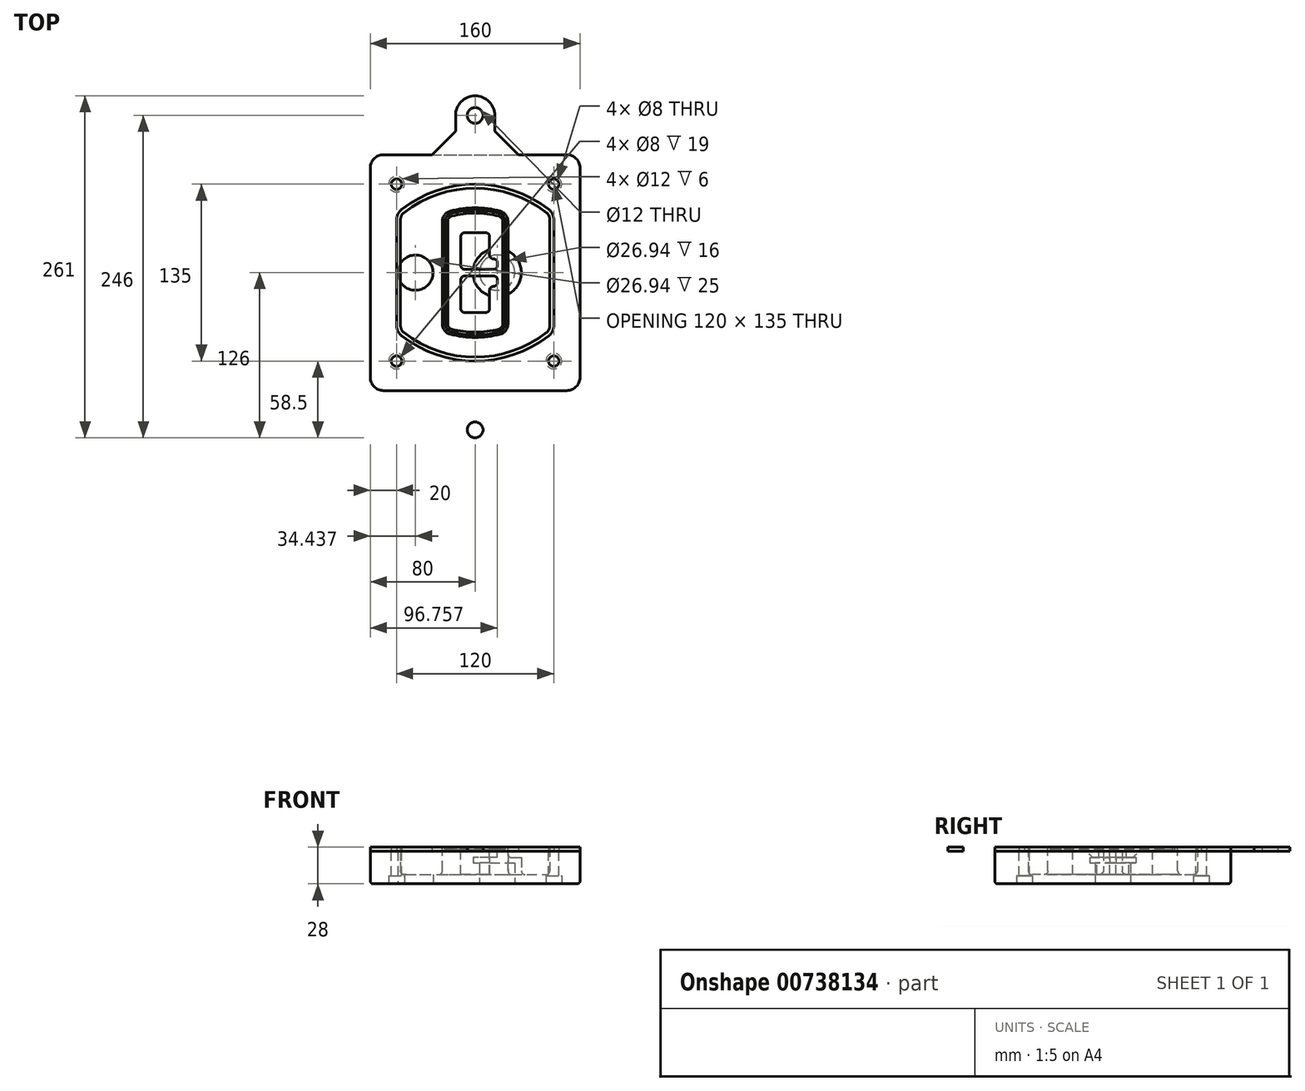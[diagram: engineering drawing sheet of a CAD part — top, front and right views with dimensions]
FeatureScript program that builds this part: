
annotation { "Feature Type Name" : "Feature", "Feature Type Description" : "" }
export const myFeature = defineFeature(function(context is Context, id is Id, definition is map)
    precondition{}
    {
        {
            var Q0;
            Q0=qCreatedBy(makeId("Top.planeOp"),FACE);
            var sketch = newSketch(context, id + "F0", { "sketchPlane" : qUnion([Q0])});
            skPoint(sketch, "E0.rect.middle", {"position": v(0, 0) * mm});
            skLineSegment(sketch, "E1.bottom", {"start": v(-70, -90) * mm, "end": v(70, -90) * mm});
            skLineSegment(sketch, "E1.top", {"start": v(-70, 90) * mm, "end": v(70, 90) * mm});
            skLineSegment(sketch, "E1.left", {"start": v(-80, -80) * mm, "end": v(-80, 80) * mm});
            skLineSegment(sketch, "E1.right", {"start": v(80, -80) * mm, "end": v(80, 80) * mm});
            skLineSegment(sketch, "E2", {"start": v(-80, 90) * mm, "end": v(80, -90) * mm, "construction": true});
            skLineSegment(sketch, "E3", {"start": v(80, 90) * mm, "end": v(-80, -90) * mm, "construction": true});
            skCircle(sketch, "E4", {"center": v(-60, 67.5) * mm, "radius": 4 * mm});
            skCircle(sketch, "E5", {"center": v(60, 67.5) * mm, "radius": 4 * mm});
            skCircle(sketch, "E6", {"center": v(60, -67.5) * mm, "radius": 4 * mm});
            skCircle(sketch, "E7", {"center": v(-60, -67.5) * mm, "radius": 4 * mm});
            skLineSegment(sketch, "E8", {"start": v(-60, 67.5) * mm, "end": v(60, 67.5) * mm, "construction": true});
            skLineSegment(sketch, "E9", {"start": v(60, 67.5) * mm, "end": v(60, -67.5) * mm, "construction": true});
            skLineSegment(sketch, "E10", {"start": v(60, -67.5) * mm, "end": v(-60, -67.5) * mm, "construction": true});
            skLineSegment(sketch, "E11", {"start": v(-60, -67.5) * mm, "end": v(-60, 67.5) * mm, "construction": true});
            skLineSegment(sketch, "E12", {"start": v(-60, 40.3) * mm, "end": v(-60, -40.3) * mm});
            skLineSegment(sketch, "E13", {"start": v(60, 40.3) * mm, "end": v(60, -40.3) * mm});
            skArc(sketch, "E14", {"start": v(56.15, 48.18) * mm, "mid": v(0, 67.5) * mm, "end": v(-56.15, 48.18) * mm});
            skArc(sketch, "E15", {"start": v(-56.15, -48.18) * mm, "mid": v(0, -67.5) * mm, "end": v(56.15, -48.18) * mm});
            skLineSegment(sketch, "E16", {"start": v(-60, 0) * mm, "end": v(60, 0) * mm, "construction": true});
            skPoint(sketch, "E17.visualSharp", {"position": v(-60, -45) * mm});
            skArc(sketch, "E17.filletArc", {"start": v(-60, -40.3) * mm, "mid": v(-58.99, -44.68) * mm, "end": v(-56.15, -48.18) * mm});
            skPoint(sketch, "E18.visualSharp", {"position": v(-60, 45) * mm});
            skArc(sketch, "E18.filletArc", {"start": v(-56.15, 48.18) * mm, "mid": v(-58.99, 44.68) * mm, "end": v(-60, 40.3) * mm});
            skPoint(sketch, "E19.visualSharp", {"position": v(60, 45) * mm});
            skArc(sketch, "E19.filletArc", {"start": v(60, 40.3) * mm, "mid": v(58.99, 44.68) * mm, "end": v(56.15, 48.18) * mm});
            skPoint(sketch, "E20.visualSharp", {"position": v(60, -45) * mm});
            skArc(sketch, "E20.filletArc", {"start": v(56.15, -48.18) * mm, "mid": v(58.99, -44.68) * mm, "end": v(60, -40.3) * mm});
            skPoint(sketch, "E21.visualSharp", {"position": v(-80, 90) * mm});
            skArc(sketch, "E21.filletArc", {"start": v(-70, 90) * mm, "mid": v(-77.07, 87.07) * mm, "end": v(-80, 80) * mm});
            skPoint(sketch, "E22.visualSharp", {"position": v(80, 90) * mm});
            skArc(sketch, "E22.filletArc", {"start": v(80, 80) * mm, "mid": v(77.07, 87.07) * mm, "end": v(70, 90) * mm});
            skPoint(sketch, "E23.visualSharp", {"position": v(80, -90) * mm});
            skArc(sketch, "E23.filletArc", {"start": v(70, -90) * mm, "mid": v(77.07, -87.07) * mm, "end": v(80, -80) * mm});
            skPoint(sketch, "E24.visualSharp", {"position": v(-80, -90) * mm});
            skArc(sketch, "E24.filletArc", {"start": v(-80, -80) * mm, "mid": v(-77.07, -87.07) * mm, "end": v(-70, -90) * mm});
            skArc(sketch, "E25.0", {"start": v(57, 40.3) * mm, "mid": v(56.3, 43.36) * mm, "end": v(54.3, 45.81) * mm});
            skLineSegment(sketch, "E25.1", {"start": v(57, 40.3) * mm, "end": v(57, -40.3) * mm});
            skArc(sketch, "E25.2", {"start": v(54.3, -45.81) * mm, "mid": v(56.3, -43.36) * mm, "end": v(57, -40.3) * mm});
            skArc(sketch, "E25.3", {"start": v(-54.3, -45.81) * mm, "mid": v(0, -64.5) * mm, "end": v(54.3, -45.81) * mm});
            skArc(sketch, "E25.4", {"start": v(-57, -40.3) * mm, "mid": v(-56.3, -43.36) * mm, "end": v(-54.3, -45.81) * mm});
            skArc(sketch, "E25.5", {"start": v(54.3, 45.81) * mm, "mid": v(0, 64.5) * mm, "end": v(-54.3, 45.81) * mm});
            skLineSegment(sketch, "E25.6", {"start": v(-57, 40.3) * mm, "end": v(-57, -40.3) * mm});
            skArc(sketch, "E25.7", {"start": v(-54.3, 45.81) * mm, "mid": v(-56.3, 43.36) * mm, "end": v(-57, 40.3) * mm});
            skArc(sketch, "E26.0", {"start": v(-58.62, 51.33) * mm, "mid": v(-62.58, 46.43) * mm, "end": v(-64, 40.3) * mm});
            skArc(sketch, "E26.1", {"start": v(58.62, 51.33) * mm, "mid": v(0, 71.5) * mm, "end": v(-58.62, 51.33) * mm});
            skArc(sketch, "E26.2", {"start": v(64, 40.3) * mm, "mid": v(62.58, 46.43) * mm, "end": v(58.62, 51.33) * mm});
            skLineSegment(sketch, "E26.3", {"start": v(64, 40.3) * mm, "end": v(64, -40.3) * mm});
            skArc(sketch, "E26.4", {"start": v(58.62, -51.33) * mm, "mid": v(62.58, -46.43) * mm, "end": v(64, -40.3) * mm});
            skLineSegment(sketch, "E26.5", {"start": v(-64, 40.3) * mm, "end": v(-64, -40.3) * mm});
            skArc(sketch, "E26.6", {"start": v(-58.62, -51.33) * mm, "mid": v(0, -71.5) * mm, "end": v(58.62, -51.33) * mm});
            skArc(sketch, "E26.7", {"start": v(-64, -40.3) * mm, "mid": v(-62.58, -46.43) * mm, "end": v(-58.62, -51.33) * mm});
            skSolve(sketch);
        }
        {
            var Q0;
            Q0=makeQuery(id+"F0.imprint","IMPRINT",FACE,{"disambiguationData":[TD([[makeQuery(id+"F0.imprint","IMPRINT",EDGE,{"derivedFrom":sQuery(id+"F0.wireOp",EDGE,"E1.bottom")}),1.0]])]});
            var Q1;
            Q1=makeQuery(id+"F0.imprint","IMPRINT",FACE,{"disambiguationData":[TD([[makeQuery(id+"F0.imprint","IMPRINT",EDGE,{"derivedFrom":sQuery(id+"F0.wireOp",EDGE,"E12")}),1.0]])]});
            var Q2;
            Q2=makeQuery(id+"F0.imprint","IMPRINT",FACE,{"disambiguationData":[TD([[makeQuery(id+"F0.imprint","IMPRINT",EDGE,{"derivedFrom":sQuery(id+"F0.wireOp",EDGE,"E25.0")}),1.0]])]});
            var Q3;
            Q3=makeQuery(id+"F0.imprint","IMPRINT",FACE,{"disambiguationData":[TD([[makeQuery(id+"F0.imprint","IMPRINT",EDGE,{"derivedFrom":sQuery(id+"F0.wireOp",EDGE,"E12")}),-1.0]])]});
            extrude(context, id + "F1", {"entities" : qUnion([Q0, Q1, Q2, Q3]), "oppositeDirection" : true, "depth" : 25 * mm});
        }
        {
            var Q0;
            Q0=makeQuery(id+"F0.imprint","IMPRINT",FACE,{"disambiguationData":[TD([[makeQuery(id+"F0.imprint","IMPRINT",EDGE,{"derivedFrom":sQuery(id+"F0.wireOp",EDGE,"E12")}),1.0]])]});
            extrude(context, id + "F2", {"entities" : qUnion([Q0]), "operationType" : NewBodyOperationType.ADD, "depth" : 3 * mm});
        }
        {
            var Q0;
            Q0=makeQuery(id+"F0.imprint","IMPRINT",FACE,{"disambiguationData":[TD([[makeQuery(id+"F0.imprint","IMPRINT",EDGE,{"derivedFrom":sQuery(id+"F0.wireOp",EDGE,"E25.0")}),1.0]])]});
            extrude(context, id + "F3", {"entities" : qUnion([Q0]), "operationType" : NewBodyOperationType.REMOVE, "oppositeDirection" : true, "depth" : 18 * mm});
        }
        {
            var Q0;
            Q0=makeQuery(id+"F2.opExtrude","CAP_FACE",FACE,{"disambiguationData":[OSD([sQuery(id+"F0.wireOp",EDGE,"E12"),sQuery(id+"F0.wireOp",EDGE,"E13"),sQuery(id+"F0.wireOp",EDGE,"E14"),sQuery(id+"F0.wireOp",EDGE,"E15"),sQuery(id+"F0.wireOp",EDGE,"E17.filletArc"),sQuery(id+"F0.wireOp",EDGE,"E18.filletArc"),sQuery(id+"F0.wireOp",EDGE,"E19.filletArc"),sQuery(id+"F0.wireOp",EDGE,"E20.filletArc"),sQuery(id+"F0.wireOp",EDGE,"E25.0"),sQuery(id+"F0.wireOp",EDGE,"E25.1"),sQuery(id+"F0.wireOp",EDGE,"E25.2"),sQuery(id+"F0.wireOp",EDGE,"E25.3"),sQuery(id+"F0.wireOp",EDGE,"E25.4"),sQuery(id+"F0.wireOp",EDGE,"E25.5"),sQuery(id+"F0.wireOp",EDGE,"E25.6"),sQuery(id+"F0.wireOp",EDGE,"E25.7")])],"isStart":false});
            var sketch = newSketch(context, id + "F4", { "sketchPlane" : qUnion([Q0])});
            skArc(sketch, "E27.0", {"start": v(-19.08, -46.97) * mm, "mid": v(0, -49.5) * mm, "end": v(19.08, -46.97) * mm});
            skArc(sketch, "E28.0", {"start": v(19.08, 46.97) * mm, "mid": v(0, 49.5) * mm, "end": v(-19.08, 46.97) * mm});
            skLineSegment(sketch, "E29", {"start": v(-25, 39.25) * mm, "end": v(-25, -39.25) * mm});
            skLineSegment(sketch, "E30", {"start": v(25, 39.25) * mm, "end": v(25, -39.25) * mm});
            skLineSegment(sketch, "E31", {"start": v(-25, 45.1) * mm, "end": v(25, 45.1) * mm, "construction": true});
            skLineSegment(sketch, "E32", {"start": v(-25, -45.1) * mm, "end": v(25, -45.1) * mm, "construction": true});
            skPoint(sketch, "E33.visualSharp", {"position": v(-25, 45.1) * mm});
            skArc(sketch, "E33.filletArc", {"start": v(-19.08, 46.97) * mm, "mid": v(-23.35, 44.11) * mm, "end": v(-25, 39.25) * mm});
            skPoint(sketch, "E34.visualSharp", {"position": v(25, 45.1) * mm});
            skArc(sketch, "E34.filletArc", {"start": v(25, 39.25) * mm, "mid": v(23.35, 44.11) * mm, "end": v(19.08, 46.97) * mm});
            skPoint(sketch, "E35.visualSharp", {"position": v(25, -45.1) * mm});
            skArc(sketch, "E35.filletArc", {"start": v(19.08, -46.97) * mm, "mid": v(23.35, -44.11) * mm, "end": v(25, -39.25) * mm});
            skPoint(sketch, "E36.visualSharp", {"position": v(-25, -45.1) * mm});
            skArc(sketch, "E36.filletArc", {"start": v(-25, -39.25) * mm, "mid": v(-23.35, -44.11) * mm, "end": v(-19.08, -46.97) * mm});
            skArc(sketch, "E37.0", {"start": v(54.3, 45.81) * mm, "mid": v(0, 64.5) * mm, "end": v(-54.3, 45.81) * mm});
            skArc(sketch, "E37.1", {"start": v(-54.3, 45.81) * mm, "mid": v(-56.3, 43.36) * mm, "end": v(-57, 40.3) * mm});
            skLineSegment(sketch, "E37.2", {"start": v(-57, 40.3) * mm, "end": v(-57, -40.3) * mm});
            skArc(sketch, "E37.3", {"start": v(-57, -40.3) * mm, "mid": v(-56.3, -43.36) * mm, "end": v(-54.3, -45.81) * mm});
            skArc(sketch, "E37.4", {"start": v(-54.3, -45.81) * mm, "mid": v(0, -64.5) * mm, "end": v(54.3, -45.81) * mm});
            skArc(sketch, "E37.5", {"start": v(54.3, -45.81) * mm, "mid": v(56.3, -43.36) * mm, "end": v(57, -40.3) * mm});
            skLineSegment(sketch, "E37.6", {"start": v(57, 40.3) * mm, "end": v(57, -40.3) * mm});
            skArc(sketch, "E37.7", {"start": v(57, 40.3) * mm, "mid": v(56.3, 43.36) * mm, "end": v(54.3, 45.81) * mm});
            skLineSegment(sketch, "E38.0", {"start": v(23, 39.25) * mm, "end": v(23, -39.25) * mm});
            skArc(sketch, "E38.1", {"start": v(18.56, -45.04) * mm, "mid": v(21.76, -42.9) * mm, "end": v(23, -39.25) * mm});
            skArc(sketch, "E38.2", {"start": v(-18.56, -45.04) * mm, "mid": v(0, -47.5) * mm, "end": v(18.56, -45.04) * mm});
            skArc(sketch, "E38.3", {"start": v(-23, -39.25) * mm, "mid": v(-21.76, -42.9) * mm, "end": v(-18.56, -45.04) * mm});
            skLineSegment(sketch, "E38.4", {"start": v(-23, 39.25) * mm, "end": v(-23, -39.25) * mm});
            skArc(sketch, "E38.5", {"start": v(23, 39.25) * mm, "mid": v(21.76, 42.9) * mm, "end": v(18.56, 45.04) * mm});
            skArc(sketch, "E38.6", {"start": v(-18.56, 45.04) * mm, "mid": v(-21.76, 42.9) * mm, "end": v(-23, 39.25) * mm});
            skArc(sketch, "E38.7", {"start": v(18.56, 45.04) * mm, "mid": v(0, 47.5) * mm, "end": v(-18.56, 45.04) * mm});
            skArc(sketch, "E39.0", {"start": v(21, 39.25) * mm, "mid": v(20.18, 41.68) * mm, "end": v(18.04, 43.1) * mm});
            skLineSegment(sketch, "E39.1", {"start": v(21, 39.25) * mm, "end": v(21, -39.25) * mm});
            skArc(sketch, "E39.2", {"start": v(18.04, -43.1) * mm, "mid": v(20.18, -41.68) * mm, "end": v(21, -39.25) * mm});
            skArc(sketch, "E39.3", {"start": v(-18.04, -43.1) * mm, "mid": v(0, -45.5) * mm, "end": v(18.04, -43.1) * mm});
            skArc(sketch, "E39.4", {"start": v(-21, -39.25) * mm, "mid": v(-20.18, -41.68) * mm, "end": v(-18.04, -43.1) * mm});
            skArc(sketch, "E39.5", {"start": v(18.04, 43.1) * mm, "mid": v(0, 45.5) * mm, "end": v(-18.04, 43.1) * mm});
            skLineSegment(sketch, "E39.6", {"start": v(-21, 39.25) * mm, "end": v(-21, -39.25) * mm});
            skArc(sketch, "E39.7", {"start": v(-18.04, 43.1) * mm, "mid": v(-20.18, 41.68) * mm, "end": v(-21, 39.25) * mm});
            skLineSegment(sketch, "E40", {"start": v(-25, 0) * mm, "end": v(25, 0) * mm, "construction": true});
            skLineSegment(sketch, "E41", {"start": v(-11, 5.5) * mm, "end": v(-11, 27.5) * mm});
            skLineSegment(sketch, "E42", {"start": v(-8, 30.5) * mm, "end": v(8, 30.5) * mm});
            skLineSegment(sketch, "E43", {"start": v(11, 27.5) * mm, "end": v(11, 13.5) * mm});
            skLineSegment(sketch, "E44", {"start": v(14, 10.5) * mm, "end": v(14, 10.5) * mm});
            skLineSegment(sketch, "E45", {"start": v(17, 7.5) * mm, "end": v(17, 5.5) * mm});
            skLineSegment(sketch, "E46", {"start": v(14, 2.5) * mm, "end": v(-8, 2.5) * mm});
            skPoint(sketch, "E47.visualSharp", {"position": v(-11, 30.5) * mm});
            skArc(sketch, "E47.filletArc", {"start": v(-8, 30.5) * mm, "mid": v(-10.12, 29.62) * mm, "end": v(-11, 27.5) * mm});
            skPoint(sketch, "E48.visualSharp", {"position": v(11, 30.5) * mm});
            skArc(sketch, "E48.filletArc", {"start": v(11, 27.5) * mm, "mid": v(10.12, 29.62) * mm, "end": v(8, 30.5) * mm});
            skPoint(sketch, "E49.visualSharp", {"position": v(11, 10.5) * mm});
            skArc(sketch, "E49.filletArc", {"start": v(11, 13.5) * mm, "mid": v(11.88, 11.38) * mm, "end": v(14, 10.5) * mm});
            skPoint(sketch, "E50.visualSharp", {"position": v(17, 10.5) * mm});
            skArc(sketch, "E50.filletArc", {"start": v(17, 7.5) * mm, "mid": v(16.12, 9.62) * mm, "end": v(14, 10.5) * mm});
            skPoint(sketch, "E51.visualSharp", {"position": v(17, 2.5) * mm});
            skArc(sketch, "E51.filletArc", {"start": v(14, 2.5) * mm, "mid": v(16.12, 3.38) * mm, "end": v(17, 5.5) * mm});
            skPoint(sketch, "E52.visualSharp", {"position": v(-11, 2.5) * mm});
            skArc(sketch, "E52.filletArc", {"start": v(-11, 5.5) * mm, "mid": v(-10.12, 3.38) * mm, "end": v(-8, 2.5) * mm});
            skLineSegment(sketch, "E53.0.MirrorCS", {"start": v(14, -2.5) * mm, "end": v(-8, -2.5) * mm});
            skArc(sketch, "E54.0.MirrorCS", {"start": v(-11, -5.5) * mm, "mid": v(-10.12, -3.38) * mm, "end": v(-8, -2.5) * mm});
            skLineSegment(sketch, "E55.0.MirrorCS", {"start": v(-11, -5.5) * mm, "end": v(-11, -27.5) * mm});
            skArc(sketch, "E56.0.MirrorCS", {"start": v(-8, -30.5) * mm, "mid": v(-10.12, -29.62) * mm, "end": v(-11, -27.5) * mm});
            skLineSegment(sketch, "E57.0.MirrorCS", {"start": v(-8, -30.5) * mm, "end": v(8, -30.5) * mm});
            skArc(sketch, "E58.0.MirrorCS", {"start": v(11, -27.5) * mm, "mid": v(10.12, -29.62) * mm, "end": v(8, -30.5) * mm});
            skLineSegment(sketch, "E59.0.MirrorCS", {"start": v(11, -27.5) * mm, "end": v(11, -13.5) * mm});
            skArc(sketch, "E60.0.MirrorCS", {"start": v(11, -13.5) * mm, "mid": v(11.88, -11.38) * mm, "end": v(14, -10.5) * mm});
            skArc(sketch, "E61.0.MirrorCS", {"start": v(17, -7.5) * mm, "mid": v(16.12, -9.62) * mm, "end": v(14, -10.5) * mm});
            skLineSegment(sketch, "E62.0.MirrorCS", {"start": v(17, -7.5) * mm, "end": v(17, -5.5) * mm});
            skArc(sketch, "E63.0.MirrorCS", {"start": v(14, -2.5) * mm, "mid": v(16.12, -3.38) * mm, "end": v(17, -5.5) * mm});
            skSolve(sketch);
        }
        {
            var Q0;
            Q0=makeQuery(id+"F4.imprint","IMPRINT",FACE,{"disambiguationData":[TD([[makeQuery(id+"F4.imprint","IMPRINT",EDGE,{"derivedFrom":sQuery(id+"F4.wireOp",EDGE,"E27.0")}),1.0]])]});
            var Q1;
            Q1=makeQuery(id+"F4.imprint","IMPRINT",FACE,{"disambiguationData":[TD([[makeQuery(id+"F4.imprint","IMPRINT",EDGE,{"derivedFrom":sQuery(id+"F4.wireOp",EDGE,"E38.0")}),-1.0]])]});
            var Q2;
            Q2=makeQuery(id+"F4.imprint","IMPRINT",FACE,{"disambiguationData":[TD([[makeQuery(id+"F4.imprint","IMPRINT",EDGE,{"derivedFrom":sQuery(id+"F4.wireOp",EDGE,"E39.0")}),1.0]])]});
            extrude(context, id + "F5", {"entities" : qUnion([Q0, Q1, Q2]), "operationType" : NewBodyOperationType.ADD, "endBound" : BoundingType.UP_TO_NEXT, "oppositeDirection" : true, "depth" : 25 * mm});
        }
        {
            var Q0;
            Q0=makeQuery(id+"F4.imprint","IMPRINT",FACE,{"disambiguationData":[TD([[makeQuery(id+"F4.imprint","IMPRINT",EDGE,{"derivedFrom":sQuery(id+"F4.wireOp",EDGE,"E38.0")}),-1.0]])]});
            extrude(context, id + "F6", {"entities" : qUnion([Q0]), "operationType" : NewBodyOperationType.REMOVE, "oppositeDirection" : true, "depth" : 2 * mm});
        }
        {
            var Q0;
            Q0=makeQuery(id+"F1.opExtrude","CAP_FACE",FACE,{"disambiguationData":[OSD([sQuery(id+"F0.wireOp",EDGE,"E1.bottom"),sQuery(id+"F0.wireOp",EDGE,"E1.top"),sQuery(id+"F0.wireOp",EDGE,"E1.left"),sQuery(id+"F0.wireOp",EDGE,"E1.right"),sQuery(id+"F0.wireOp",EDGE,"E4"),sQuery(id+"F0.wireOp",EDGE,"E5"),sQuery(id+"F0.wireOp",EDGE,"E6"),sQuery(id+"F0.wireOp",EDGE,"E7"),sQuery(id+"F0.wireOp",EDGE,"E21.filletArc"),sQuery(id+"F0.wireOp",EDGE,"E22.filletArc"),sQuery(id+"F0.wireOp",EDGE,"E23.filletArc"),sQuery(id+"F0.wireOp",EDGE,"E24.filletArc")])],"isStart":false});
            var sketch = newSketch(context, id + "F7", { "sketchPlane" : qUnion([Q0])});
            skCircle(sketch, "E64", {"center": v(16.76, 0) * mm, "radius": 13.47 * mm});
            skCircle(sketch, "E65", {"center": v(-45.56, 0) * mm, "radius": 13.47 * mm});
            skLineSegment(sketch, "E66", {"start": v(80, 0) * mm, "end": v(-80, 0) * mm});
            skCircle(sketch, "E67", {"center": v(16.76, 0) * mm, "radius": 18.47 * mm});
            skCircle(sketch, "E68", {"center": v(60, -67.5) * mm, "radius": 6 * mm});
            skCircle(sketch, "E69", {"center": v(-60, -67.5) * mm, "radius": 6 * mm});
            skCircle(sketch, "E70", {"center": v(-60, 67.5) * mm, "radius": 6 * mm});
            skCircle(sketch, "E71", {"center": v(60, 67.5) * mm, "radius": 6 * mm});
            skSolve(sketch);
        }
        {
            var Q0;
            {var subQ1=sQuery(id+"F7.wireOp",EDGE,"E66");var subQ4=sQuery(id+"F7.wireOp",EDGE,"E64");var subQ6=makeQuery(id+"F7.imprint","INTERSECT",VERTEX,{"disambiguationData":[OD(0.0)],"derivedFrom":[subQ4,subQ1]});Q0=makeQuery(id+"F7.imprint","IMPRINT",FACE,{"disambiguationData":[TD([[makeQuery(id+"F7.imprint","IMPRINT",EDGE,{"disambiguationData":[TD([[subQ6,-1.0]])],"derivedFrom":subQ4}),-1.0]])]});}
            var Q1;
            {var subQ0=sQuery(id+"F7.wireOp",EDGE,"E66");var subQ1=sQuery(id+"F7.wireOp",EDGE,"E64");var subQ3=makeQuery(id+"F7.imprint","INTERSECT",VERTEX,{"disambiguationData":[OD(0.0)],"derivedFrom":[subQ1,subQ0]});Q1=makeQuery(id+"F7.imprint","IMPRINT",FACE,{"disambiguationData":[TD([[makeQuery(id+"F7.imprint","IMPRINT",EDGE,{"disambiguationData":[TD([[subQ3,-1.0]])],"derivedFrom":subQ1}),1.0]])]});}
            var Q2;
            {var subQ0=sQuery(id+"F7.wireOp",EDGE,"E66");var subQ1=sQuery(id+"F7.wireOp",EDGE,"E64");var subQ3=makeQuery(id+"F7.imprint","INTERSECT",VERTEX,{"disambiguationData":[OD(0.0)],"derivedFrom":[subQ1,subQ0]});Q2=makeQuery(id+"F7.imprint","IMPRINT",FACE,{"disambiguationData":[TD([[makeQuery(id+"F7.imprint","IMPRINT",EDGE,{"disambiguationData":[TD([[subQ3,1.0]])],"derivedFrom":subQ1}),1.0]])]});}
            var Q3;
            {var subQ1=sQuery(id+"F7.wireOp",EDGE,"E66");var subQ4=sQuery(id+"F7.wireOp",EDGE,"E64");var subQ6=makeQuery(id+"F7.imprint","INTERSECT",VERTEX,{"disambiguationData":[OD(0.0)],"derivedFrom":[subQ4,subQ1]});Q3=makeQuery(id+"F7.imprint","IMPRINT",FACE,{"disambiguationData":[TD([[makeQuery(id+"F7.imprint","IMPRINT",EDGE,{"disambiguationData":[TD([[subQ6,1.0]])],"derivedFrom":subQ4}),-1.0]])]});}
            extrude(context, id + "F8", {"entities" : qUnion([Q0, Q1, Q2, Q3]), "operationType" : NewBodyOperationType.ADD, "oppositeDirection" : true, "depth" : 20 * mm});
        }
        {
            var Q0;
            {var subQ0=sQuery(id+"F7.wireOp",EDGE,"E66");var subQ1=sQuery(id+"F7.wireOp",EDGE,"E64");var subQ3=makeQuery(id+"F7.imprint","INTERSECT",VERTEX,{"disambiguationData":[OD(0.0)],"derivedFrom":[subQ1,subQ0]});Q0=makeQuery(id+"F7.imprint","IMPRINT",FACE,{"disambiguationData":[TD([[makeQuery(id+"F7.imprint","IMPRINT",EDGE,{"disambiguationData":[TD([[subQ3,-1.0]])],"derivedFrom":subQ1}),1.0]])]});}
            var Q1;
            {var subQ0=sQuery(id+"F7.wireOp",EDGE,"E66");var subQ1=sQuery(id+"F7.wireOp",EDGE,"E64");var subQ3=makeQuery(id+"F7.imprint","INTERSECT",VERTEX,{"disambiguationData":[OD(0.0)],"derivedFrom":[subQ1,subQ0]});Q1=makeQuery(id+"F7.imprint","IMPRINT",FACE,{"disambiguationData":[TD([[makeQuery(id+"F7.imprint","IMPRINT",EDGE,{"disambiguationData":[TD([[subQ3,1.0]])],"derivedFrom":subQ1}),1.0]])]});}
            extrude(context, id + "F9", {"entities" : qUnion([Q0, Q1]), "operationType" : NewBodyOperationType.REMOVE, "oppositeDirection" : true, "depth" : 16 * mm});
        }
        {
            var Q0;
            {var subQ0=sQuery(id+"F7.wireOp",EDGE,"E66");var subQ1=sQuery(id+"F7.wireOp",EDGE,"E65");var subQ3=makeQuery(id+"F7.imprint","INTERSECT",VERTEX,{"disambiguationData":[OD(0.0)],"derivedFrom":[subQ1,subQ0]});Q0=makeQuery(id+"F7.imprint","IMPRINT",FACE,{"disambiguationData":[TD([[makeQuery(id+"F7.imprint","IMPRINT",EDGE,{"disambiguationData":[TD([[subQ3,-1.0]])],"derivedFrom":subQ1}),1.0]])]});}
            var Q1;
            {var subQ0=sQuery(id+"F7.wireOp",EDGE,"E66");var subQ1=sQuery(id+"F7.wireOp",EDGE,"E65");var subQ3=makeQuery(id+"F7.imprint","INTERSECT",VERTEX,{"disambiguationData":[OD(0.0)],"derivedFrom":[subQ1,subQ0]});Q1=makeQuery(id+"F7.imprint","IMPRINT",FACE,{"disambiguationData":[TD([[makeQuery(id+"F7.imprint","IMPRINT",EDGE,{"disambiguationData":[TD([[subQ3,1.0]])],"derivedFrom":subQ1}),1.0]])]});}
            extrude(context, id + "F10", {"entities" : qUnion([Q0, Q1]), "operationType" : NewBodyOperationType.REMOVE, "oppositeDirection" : true, "depth" : 25 * mm});
        }
        {
            var Q0;
            Q0=makeQuery(id+"F7.imprint","IMPRINT",FACE,{"disambiguationData":[TD([[makeQuery(id+"F7.imprint","IMPRINT",EDGE,{"derivedFrom":sQuery(id+"F7.wireOp",EDGE,"E68")}),1.0]])]});
            var Q1;
            Q1=makeQuery(id+"F7.imprint","IMPRINT",FACE,{"disambiguationData":[TD([[makeQuery(id+"F7.imprint","IMPRINT",EDGE,{"derivedFrom":makeQuery(id+"F1.opExtrude","CAP_EDGE",EDGE,{"disambiguationData":[OSD([sQuery(id+"F0.wireOp",EDGE,"E5")])],"isStart":false})}),-1.0]])]});
            var Q2;
            Q2=makeQuery(id+"F7.imprint","IMPRINT",FACE,{"disambiguationData":[TD([[makeQuery(id+"F7.imprint","IMPRINT",EDGE,{"derivedFrom":sQuery(id+"F7.wireOp",EDGE,"E69")}),1.0]])]});
            var Q3;
            Q3=makeQuery(id+"F7.imprint","IMPRINT",FACE,{"disambiguationData":[TD([[makeQuery(id+"F7.imprint","IMPRINT",EDGE,{"derivedFrom":makeQuery(id+"F1.opExtrude","CAP_EDGE",EDGE,{"disambiguationData":[OSD([sQuery(id+"F0.wireOp",EDGE,"E4")])],"isStart":false})}),-1.0]])]});
            var Q4;
            Q4=makeQuery(id+"F7.imprint","IMPRINT",FACE,{"disambiguationData":[TD([[makeQuery(id+"F7.imprint","IMPRINT",EDGE,{"derivedFrom":sQuery(id+"F7.wireOp",EDGE,"E70")}),1.0]])]});
            var Q5;
            Q5=makeQuery(id+"F7.imprint","IMPRINT",FACE,{"disambiguationData":[TD([[makeQuery(id+"F7.imprint","IMPRINT",EDGE,{"derivedFrom":makeQuery(id+"F1.opExtrude","CAP_EDGE",EDGE,{"disambiguationData":[OSD([sQuery(id+"F0.wireOp",EDGE,"E7")])],"isStart":false})}),-1.0]])]});
            var Q6;
            Q6=makeQuery(id+"F7.imprint","IMPRINT",FACE,{"disambiguationData":[TD([[makeQuery(id+"F7.imprint","IMPRINT",EDGE,{"derivedFrom":sQuery(id+"F7.wireOp",EDGE,"E71")}),1.0]])]});
            var Q7;
            Q7=makeQuery(id+"F7.imprint","IMPRINT",FACE,{"disambiguationData":[TD([[makeQuery(id+"F7.imprint","IMPRINT",EDGE,{"derivedFrom":makeQuery(id+"F1.opExtrude","CAP_EDGE",EDGE,{"disambiguationData":[OSD([sQuery(id+"F0.wireOp",EDGE,"E6")])],"isStart":false})}),-1.0]])]});
            extrude(context, id + "F11", {"entities" : qUnion([Q0, Q1, Q2, Q3, Q4, Q5, Q6, Q7]), "operationType" : NewBodyOperationType.REMOVE, "oppositeDirection" : true, "depth" : 6 * mm});
        }
        {
            var Q0;
            Q0=makeQuery(id+"F9.boolean.opBoolean","COPY",FACE,{"derivedFrom":makeQuery(id+"F9.opExtrude","CAP_FACE",FACE,{"disambiguationData":[OSD([sQuery(id+"F7.wireOp",EDGE,"E64")])],"isStart":false})});
            var sketch = newSketch(context, id + "F12", { "sketchPlane" : qUnion([Q0])});
            skArc(sketch, "E72.0", {"start": v(11, 17.55) * mm, "mid": v(2.57, 11.82) * mm, "end": v(-1.54, 2.5) * mm});
            skArc(sketch, "E72.1", {"start": v(-1.54, -2.5) * mm, "mid": v(2.57, -11.82) * mm, "end": v(11, -17.55) * mm});
            skLineSegment(sketch, "E73", {"start": v(-1.54, -2.5) * mm, "end": v(14, -2.5) * mm});
            skLineSegment(sketch, "E74.0", {"start": v(14, 2.5) * mm, "end": v(-1.54, 2.5) * mm});
            skArc(sketch, "E74.1", {"start": v(14, 2.5) * mm, "mid": v(16.12, 3.38) * mm, "end": v(17, 5.5) * mm});
            skLineSegment(sketch, "E74.2", {"start": v(17, 7.5) * mm, "end": v(17, 5.5) * mm});
            skArc(sketch, "E74.3", {"start": v(17, 7.5) * mm, "mid": v(16.12, 9.62) * mm, "end": v(14, 10.5) * mm});
            skArc(sketch, "E74.4", {"start": v(11, 13.5) * mm, "mid": v(11.88, 11.38) * mm, "end": v(14, 10.5) * mm});
            skLineSegment(sketch, "E74.5", {"start": v(11, 17.55) * mm, "end": v(11, 13.5) * mm});
            skLineSegment(sketch, "E74.7", {"start": v(14, -2.5) * mm, "end": v(-1.54, -2.5) * mm});
            skArc(sketch, "E74.8", {"start": v(14, -2.5) * mm, "mid": v(16.12, -3.38) * mm, "end": v(17, -5.5) * mm});
            skLineSegment(sketch, "E74.9", {"start": v(17, -7.5) * mm, "end": v(17, -5.5) * mm});
            skArc(sketch, "E74.10", {"start": v(17, -7.5) * mm, "mid": v(16.12, -9.62) * mm, "end": v(14, -10.5) * mm});
            skArc(sketch, "E74.11", {"start": v(11, -13.5) * mm, "mid": v(11.88, -11.38) * mm, "end": v(14, -10.5) * mm});
            skLineSegment(sketch, "E74.12", {"start": v(11, -17.55) * mm, "end": v(11, -13.5) * mm});
            skPoint(sketch, "E75.orphan", {"position": v(11, -27.5) * mm});
            skPoint(sketch, "E76.orphan", {"position": v(-8, -2.5) * mm});
            skPoint(sketch, "E77.orphan", {"position": v(-8, 2.5) * mm});
            skPoint(sketch, "E78.orphan", {"position": v(11, 27.5) * mm});
            skSolve(sketch);
        }
        {
            var Q0;
            {var subQ7=sQuery(id+"F12.wireOp",EDGE,"E72.0");var subQ14=sQuery(id+"F12.wireOp",EDGE,"E72.1");var subQ16=sQuery(id+"F12.wireOp",EDGE,"E74.1");var subQ18=sQuery(id+"F12.wireOp",EDGE,"E74.8");Q0=qUnion([makeQuery(id+"F12.imprint","IMPRINT",FACE,{"disambiguationData":[TD([[makeQuery(id+"F12.imprint","IMPRINT",EDGE,{"derivedFrom":subQ7}),1.0]])]}),makeQuery(id+"F12.imprint","IMPRINT",FACE,{"disambiguationData":[TD([[makeQuery(id+"F12.imprint","IMPRINT",EDGE,{"derivedFrom":subQ14}),1.0]])]}),makeQuery(id+"F12.imprint","IMPRINT",FACE,{"disambiguationData":[TD([[makeQuery(id+"F12.imprint","IMPRINT",EDGE,{"derivedFrom":subQ16}),1.0]])]}),makeQuery(id+"F12.imprint","IMPRINT",FACE,{"disambiguationData":[TD([[makeQuery(id+"F12.imprint","IMPRINT",EDGE,{"derivedFrom":subQ18}),-1.0]])]})]);}
            var Q1;
            Q1=makeQuery(id+"F5.boolean.opBoolean","SPLIT",FACE,{"disambiguationData":[TD([makeQuery(id+"F5.opExtrude","SWEPT_FACE",FACE,{"disambiguationData":[OSD([sQuery(id+"F4.wireOp",EDGE,"E41")])]})])],"derivedFrom":makeQuery(id+"F3.boolean.opBoolean","COPY",FACE,{"derivedFrom":makeQuery(id+"F3.opExtrude","CAP_FACE",FACE,{"disambiguationData":[OSD([sQuery(id+"F0.wireOp",EDGE,"E25.0"),sQuery(id+"F0.wireOp",EDGE,"E25.1"),sQuery(id+"F0.wireOp",EDGE,"E25.2"),sQuery(id+"F0.wireOp",EDGE,"E25.3"),sQuery(id+"F0.wireOp",EDGE,"E25.4"),sQuery(id+"F0.wireOp",EDGE,"E25.5"),sQuery(id+"F0.wireOp",EDGE,"E25.6"),sQuery(id+"F0.wireOp",EDGE,"E25.7")])],"isStart":false})})});
            extrude(context, id + "F13", {"entities" : qUnion([Q0]), "operationType" : NewBodyOperationType.REMOVE, "endBound" : BoundingType.UP_TO_SURFACE, "endBoundEntityFace" : qUnion([Q1]), "depth" : 25 * mm});
        }
        {
            var Q0;
            Q0=makeQuery(id+"F3.boolean.opBoolean","COPY",EDGE,{"derivedFrom":makeQuery(id+"F3.opExtrude","CAP_EDGE",EDGE,{"disambiguationData":[OSD([sQuery(id+"F0.wireOp",EDGE,"E25.6")])],"isStart":false})});
            var Q1;
            Q1=makeQuery(id+"F8.boolean.opBoolean","INTERSECT",EDGE,{"derivedFrom":[makeQuery(id+"F5.opExtrude","SWEPT_FACE",FACE,{"disambiguationData":[OSD([sQuery(id+"F4.wireOp",EDGE,"E30")])]}),makeQuery(id+"F8.opExtrude","CAP_FACE",FACE,{"disambiguationData":[OSD([sQuery(id+"F7.wireOp",EDGE,"E67")])],"isStart":false})]});
            var Q2;
            Q2=makeQuery(id+"F8.boolean.opBoolean","INTERSECT",EDGE,{"disambiguationData":[OD(1.0)],"derivedFrom":[makeQuery(id+"F5.opExtrude","SWEPT_FACE",FACE,{"disambiguationData":[OSD([sQuery(id+"F4.wireOp",EDGE,"E30")])]}),makeQuery(id+"F8.opExtrude","SWEPT_FACE",FACE,{"disambiguationData":[OSD([sQuery(id+"F7.wireOp",EDGE,"E67")])]})]});
            var Q3;
            {var subQ0=sQuery(id+"F4.wireOp",EDGE,"E30");Q3=makeQuery(id+"F8.boolean.opBoolean","SPLIT",EDGE,{"disambiguationData":[TD([makeQuery(id+"F5.opExtrude","SWEPT_FACE",FACE,{"disambiguationData":[OSD([sQuery(id+"F4.wireOp",EDGE,"E35.filletArc")])]})])],"derivedFrom":makeQuery(id+"F5.opExtrude","CAP_EDGE",EDGE,{"disambiguationData":[OSD([subQ0])],"isStart":false})});}
            var Q4;
            {var subQ0=sQuery(id+"F0.wireOp",EDGE,"E25.7");var subQ1=sQuery(id+"F0.wireOp",EDGE,"E25.1");var subQ2=sQuery(id+"F0.wireOp",EDGE,"E25.6");var subQ3=sQuery(id+"F0.wireOp",EDGE,"E25.5");var subQ4=sQuery(id+"F0.wireOp",EDGE,"E25.4");var subQ5=sQuery(id+"F0.wireOp",EDGE,"E25.0");var subQ6=sQuery(id+"F0.wireOp",EDGE,"E25.2");var subQ7=sQuery(id+"F0.wireOp",EDGE,"E25.3");Q4=makeQuery(id+"F8.boolean.opBoolean","INTERSECT",EDGE,{"derivedFrom":[makeQuery(id+"F5.boolean.opBoolean","SPLIT",FACE,{"disambiguationData":[TD([makeQuery(id+"F2.opExtrude","SWEPT_FACE",FACE,{"disambiguationData":[OSD([subQ5])]})])],"derivedFrom":makeQuery(id+"F3.boolean.opBoolean","COPY",FACE,{"derivedFrom":makeQuery(id+"F3.opExtrude","CAP_FACE",FACE,{"disambiguationData":[OSD([subQ5,subQ1,subQ6,subQ7,subQ4,subQ3,subQ2,subQ0])],"isStart":false})})}),makeQuery(id+"F8.opExtrude","SWEPT_FACE",FACE,{"disambiguationData":[OSD([sQuery(id+"F7.wireOp",EDGE,"E67")])]})]});}
            var Q5;
            Q5=makeQuery(id+"F8.boolean.opBoolean","INTERSECT",EDGE,{"disambiguationData":[OD(0.0)],"derivedFrom":[makeQuery(id+"F5.opExtrude","SWEPT_FACE",FACE,{"disambiguationData":[OSD([sQuery(id+"F4.wireOp",EDGE,"E30")])]}),makeQuery(id+"F8.opExtrude","SWEPT_FACE",FACE,{"disambiguationData":[OSD([sQuery(id+"F7.wireOp",EDGE,"E67")])]})]});
            fillet(context, id + "F14", {"entities" : qUnion([Q0, Q1, Q2, Q3, Q4, Q5]), "radius" : 3 * mm, "tangentPropagation" : true, "allowEdgeOverflow" : false});
        }
        {
            var Q0;
            Q0=makeQuery(id+"F1.opExtrude","CAP_EDGE",EDGE,{"disambiguationData":[OSD([sQuery(id+"F0.wireOp",EDGE,"E1.bottom")])],"isStart":false});
            fillet(context, id + "F15", {"entities" : qUnion([Q0]), "radius" : 2 * mm, "tangentPropagation" : true, "allowEdgeOverflow" : false});
        }
        {
            var Q0;
            {var subQ0=sQuery(id+"F0.wireOp",EDGE,"E21.filletArc");var subQ1=sQuery(id+"F0.wireOp",EDGE,"E7");var subQ2=sQuery(id+"F0.wireOp",EDGE,"E6");var subQ3=sQuery(id+"F0.wireOp",EDGE,"E5");var subQ4=sQuery(id+"F0.wireOp",EDGE,"E4");var subQ5=sQuery(id+"F0.wireOp",EDGE,"E22.filletArc");var subQ6=sQuery(id+"F0.wireOp",EDGE,"E1.bottom");var subQ7=sQuery(id+"F0.wireOp",EDGE,"E1.right");var subQ8=sQuery(id+"F0.wireOp",EDGE,"E1.top");var subQ9=sQuery(id+"F0.wireOp",EDGE,"E1.left");var subQ10=sQuery(id+"F0.wireOp",EDGE,"E23.filletArc");var subQ11=sQuery(id+"F0.wireOp",EDGE,"E24.filletArc");Q0=makeQuery(id+"F2.boolean.opBoolean","SPLIT",FACE,{"disambiguationData":[TD([makeQuery(id+"F1.opExtrude","SWEPT_FACE",FACE,{"disambiguationData":[OSD([subQ6])]})])],"derivedFrom":makeQuery(id+"F1.opExtrude","CAP_FACE",FACE,{"disambiguationData":[OSD([subQ6,subQ8,subQ9,subQ7,subQ4,subQ3,subQ2,subQ1,subQ0,subQ5,subQ10,subQ11])],"isStart":true})});}
            var sketch = newSketch(context, id + "F16", { "sketchPlane" : qUnion([Q0])});
            skLineSegment(sketch, "E79.0", {"start": v(-70, 90) * mm, "end": v(70, 90) * mm});
            skArc(sketch, "E79.1", {"start": v(-70, 90) * mm, "mid": v(-77.07, 87.07) * mm, "end": v(-80, 80) * mm});
            skLineSegment(sketch, "E79.2", {"start": v(-80, -80) * mm, "end": v(-80, 80) * mm});
            skArc(sketch, "E79.3", {"start": v(-80, -80) * mm, "mid": v(-77.07, -87.07) * mm, "end": v(-70, -90) * mm});
            skLineSegment(sketch, "E79.4", {"start": v(-70, -90) * mm, "end": v(70, -90) * mm});
            skArc(sketch, "E79.5", {"start": v(70, -90) * mm, "mid": v(77.07, -87.07) * mm, "end": v(80, -80) * mm});
            skLineSegment(sketch, "E79.6", {"start": v(80, -80) * mm, "end": v(80, 80) * mm});
            skArc(sketch, "E79.7", {"start": v(80, 80) * mm, "mid": v(77.07, 87.07) * mm, "end": v(70, 90) * mm});
            skPoint(sketch, "E79.8", {"position": v(80, 80) * mm});
            skPoint(sketch, "E79.9", {"position": v(70, 90) * mm});
            skPoint(sketch, "E79.10", {"position": v(-70, 90) * mm});
            skPoint(sketch, "E79.11", {"position": v(-80, 80) * mm});
            skPoint(sketch, "E79.12", {"position": v(-80, -80) * mm});
            skPoint(sketch, "E79.13", {"position": v(-70, -90) * mm});
            skCircle(sketch, "E79.14", {"center": v(-60, -67.5) * mm, "radius": 4 * mm});
            skCircle(sketch, "E79.15", {"center": v(60, -67.5) * mm, "radius": 4 * mm});
            skPoint(sketch, "E79.16", {"position": v(70, -90) * mm});
            skPoint(sketch, "E79.17", {"position": v(80, -80) * mm});
            skCircle(sketch, "E79.18", {"center": v(60, 67.5) * mm, "radius": 4 * mm});
            skCircle(sketch, "E79.19", {"center": v(-60, 67.5) * mm, "radius": 4 * mm});
            skArc(sketch, "E79.20", {"start": v(56.15, 48.18) * mm, "mid": v(0, 67.5) * mm, "end": v(-56.15, 48.18) * mm});
            skArc(sketch, "E79.21", {"start": v(60, 40.3) * mm, "mid": v(58.99, 44.68) * mm, "end": v(56.15, 48.18) * mm});
            skLineSegment(sketch, "E79.22", {"start": v(60, 40.3) * mm, "end": v(60, -40.3) * mm});
            skArc(sketch, "E79.23", {"start": v(56.15, -48.18) * mm, "mid": v(58.99, -44.68) * mm, "end": v(60, -40.3) * mm});
            skArc(sketch, "E79.24", {"start": v(-56.15, -48.18) * mm, "mid": v(0, -67.5) * mm, "end": v(56.15, -48.18) * mm});
            skLineSegment(sketch, "E79.25", {"start": v(-60, 40.3) * mm, "end": v(-60, -40.3) * mm});
            skArc(sketch, "E79.26", {"start": v(-56.15, 48.18) * mm, "mid": v(-58.99, 44.68) * mm, "end": v(-60, 40.3) * mm});
            skArc(sketch, "E79.27", {"start": v(-60, -40.3) * mm, "mid": v(-58.99, -44.68) * mm, "end": v(-56.15, -48.18) * mm});
            skLineSegment(sketch, "E80", {"start": v(33, 90) * mm, "end": v(15, 108) * mm});
            skLineSegment(sketch, "E81", {"start": v(15, 108) * mm, "end": v(15, 120) * mm});
            skLineSegment(sketch, "E82", {"start": v(-33, 90) * mm, "end": v(-15, 108) * mm});
            skLineSegment(sketch, "E83", {"start": v(-15, 108) * mm, "end": v(-15, 120) * mm});
            skArc(sketch, "E84", {"start": v(15, 120) * mm, "mid": v(0, 135) * mm, "end": v(-15, 120) * mm});
            skCircle(sketch, "E85", {"center": v(0, 120) * mm, "radius": 6 * mm});
            skLineSegment(sketch, "E86", {"start": v(0, 23.75) * mm, "end": v(0, 120) * mm, "construction": true});
            skLineSegment(sketch, "E87", {"start": v(-80, 0) * mm, "end": v(80, 0) * mm, "construction": true});
            skCircle(sketch, "E88.MirrorC", {"center": v(0, -120) * mm, "radius": 6 * mm});
            skArc(sketch, "E89.MirrorCS", {"start": v(80, -80) * mm, "mid": v(77.07, -87.07) * mm, "end": v(70, -90) * mm});
            skArc(sketch, "E90.MirrorCS", {"start": v(-70, -90) * mm, "mid": v(-77.07, -87.07) * mm, "end": v(-80, -80) * mm});
            skLineSegment(sketch, "E91.MirrorCS", {"start": v(-15, -108) * mm, "end": v(-15, -120) * mm});
            skLineSegment(sketch, "E92.MirrorCS", {"start": v(15, -108) * mm, "end": v(15, -120) * mm});
            skArc(sketch, "E93.MirrorCS", {"start": v(-56.15, -48.18) * mm, "mid": v(-58.99, -44.68) * mm, "end": v(-60, -40.3) * mm});
            skArc(sketch, "E94.MirrorCS", {"start": v(60, -40.3) * mm, "mid": v(58.99, -44.68) * mm, "end": v(56.15, -48.18) * mm});
            skLineSegment(sketch, "E95.MirrorCS", {"start": v(-33, -90) * mm, "end": v(-15, -108) * mm});
            skLineSegment(sketch, "E96.MirrorCS", {"start": v(33, -90) * mm, "end": v(15, -108) * mm});
            skLineSegment(sketch, "E97.MirrorCS", {"start": v(0, -23.75) * mm, "end": v(0, -120) * mm, "construction": true});
            skArc(sketch, "E98.MirrorCS", {"start": v(56.15, -48.18) * mm, "mid": v(0, -67.5) * mm, "end": v(-56.15, -48.18) * mm});
            skArc(sketch, "E99.MirrorCS", {"start": v(15, -120) * mm, "mid": v(0, -135) * mm, "end": v(-15, -120) * mm});
            skSolve(sketch);
        }
        {
            var Q0;
            Q0=makeQuery(id+"F16.imprint","IMPRINT",FACE,{"disambiguationData":[TD([[makeQuery(id+"F16.imprint","IMPRINT",EDGE,{"derivedFrom":sQuery(id+"F16.wireOp",EDGE,"E88.MirrorC")}),1.0]])]});
            var Q1;
            {var subQ4=sQuery(id+"F16.wireOp",EDGE,"E79.1");Q1=makeQuery(id+"F16.imprint","IMPRINT",FACE,{"disambiguationData":[TD([[makeQuery(id+"F16.imprint","IMPRINT",EDGE,{"derivedFrom":subQ4}),1.0]])]});}
            var Q2;
            {var subQ0=sQuery(id+"F16.wireOp",EDGE,"E80");Q2=makeQuery(id+"F16.imprint","IMPRINT",FACE,{"disambiguationData":[TD([[makeQuery(id+"F16.imprint","IMPRINT",EDGE,{"derivedFrom":subQ0}),1.0]])]});}
            var Q3;
            Q3=makeQuery(id+"F2.opExtrude","CAP_FACE",FACE,{"disambiguationData":[OSD([sQuery(id+"F0.wireOp",EDGE,"E12"),sQuery(id+"F0.wireOp",EDGE,"E13"),sQuery(id+"F0.wireOp",EDGE,"E14"),sQuery(id+"F0.wireOp",EDGE,"E15"),sQuery(id+"F0.wireOp",EDGE,"E17.filletArc"),sQuery(id+"F0.wireOp",EDGE,"E18.filletArc"),sQuery(id+"F0.wireOp",EDGE,"E19.filletArc"),sQuery(id+"F0.wireOp",EDGE,"E20.filletArc"),sQuery(id+"F0.wireOp",EDGE,"E25.0"),sQuery(id+"F0.wireOp",EDGE,"E25.1"),sQuery(id+"F0.wireOp",EDGE,"E25.2"),sQuery(id+"F0.wireOp",EDGE,"E25.3"),sQuery(id+"F0.wireOp",EDGE,"E25.4"),sQuery(id+"F0.wireOp",EDGE,"E25.5"),sQuery(id+"F0.wireOp",EDGE,"E25.6"),sQuery(id+"F0.wireOp",EDGE,"E25.7")])],"isStart":false});
            extrude(context, id + "F17", {"entities" : qUnion([Q0, Q1, Q2]), "endBound" : BoundingType.UP_TO_SURFACE, "depth" : 25 * mm, "endBoundEntityFace" : qUnion([Q3]), "offsetDistance" : 25 * mm});
        }
    });
